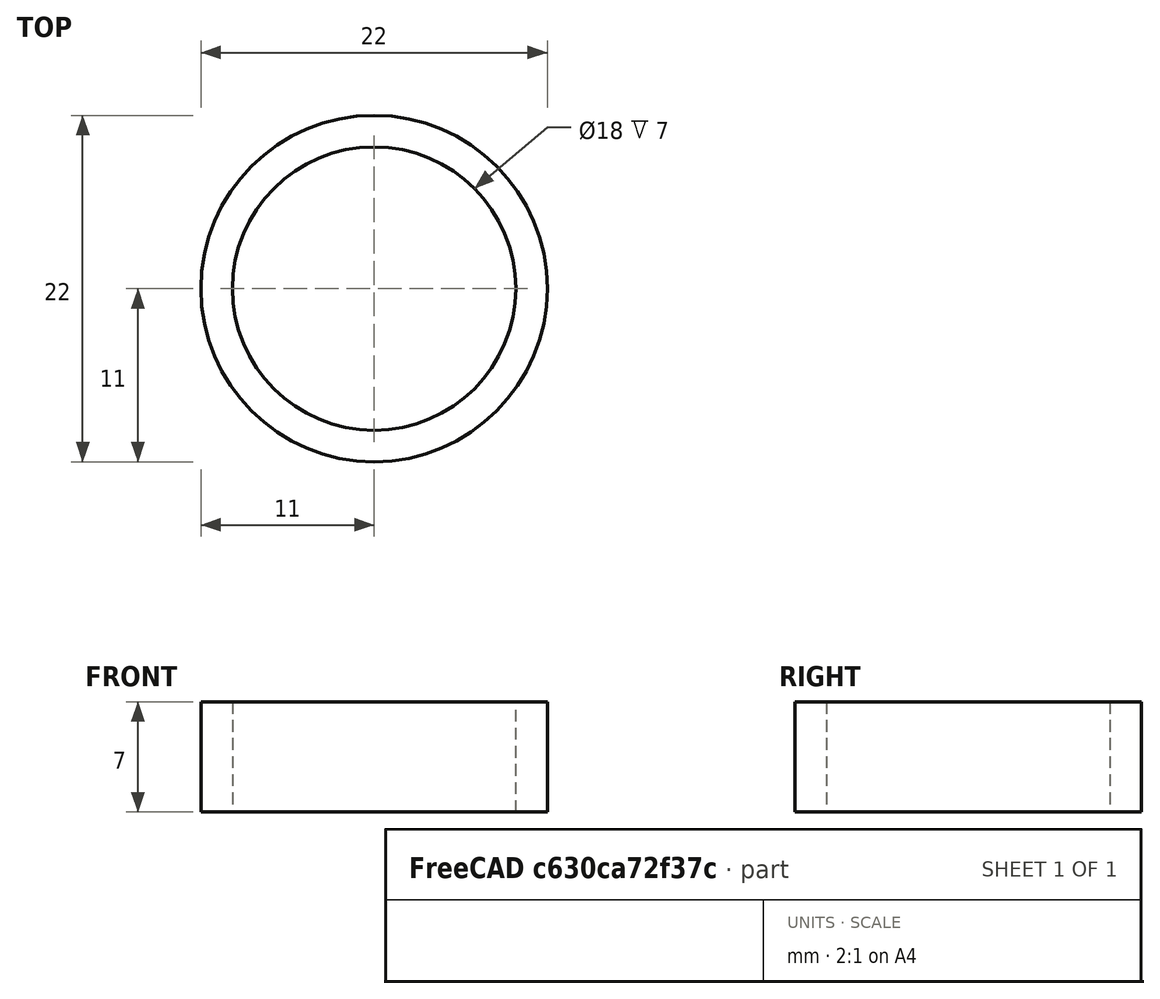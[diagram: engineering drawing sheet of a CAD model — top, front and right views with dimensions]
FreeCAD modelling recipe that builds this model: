
FCSTD DOCUMENT  (FreeCAD 0.19R24276 (Git))
Label: podshipnik_22x8x7_out_ring
License: All rights reserved
LicenseURL: http://en.wikipedia.org/wiki/All_rights_reserved
objects: Sketcher::SketchObject×1, PartDesign::Pad×1, PartDesign::Body×1
note: 4 computed .brp shape members not serialized (recipe doc carries the construction recipe); baked Part::Feature solids carry a one-line shape summary decoded from their .brp

FEATURE [Sketcher::SketchObject] Sketch
  FullyConstrained = true
  MapMode = 5
  Support = -> [XY_Plane]
  sketch-geometry (2):
    g0: Circle CenterX=0 CenterY=0 CenterZ=0 NormalX=0 NormalY=0 NormalZ=1 AngleXU=0 Radius=11
    g1: Circle CenterX=0 CenterY=0 CenterZ=0 NormalX=0 NormalY=0 NormalZ=1 AngleXU=0 Radius=9
  constraints (4):
    c: Coincident(g0,g-1)
    c: Coincident(g1,g0)
    c: Diameter(g0) = 22
    c: Diameter(g1) = 18
FEATURE [PartDesign::Pad] Pad
  Direction = (1,1,1)
  Length = 7
  Length2 = 100
  Profile = -> Sketch
  Type = 0
FEATURE [PartDesign::Body] Body
  Group = -> [Sketch,Pad]
  Origin = -> Origin
  Tip = -> Pad
